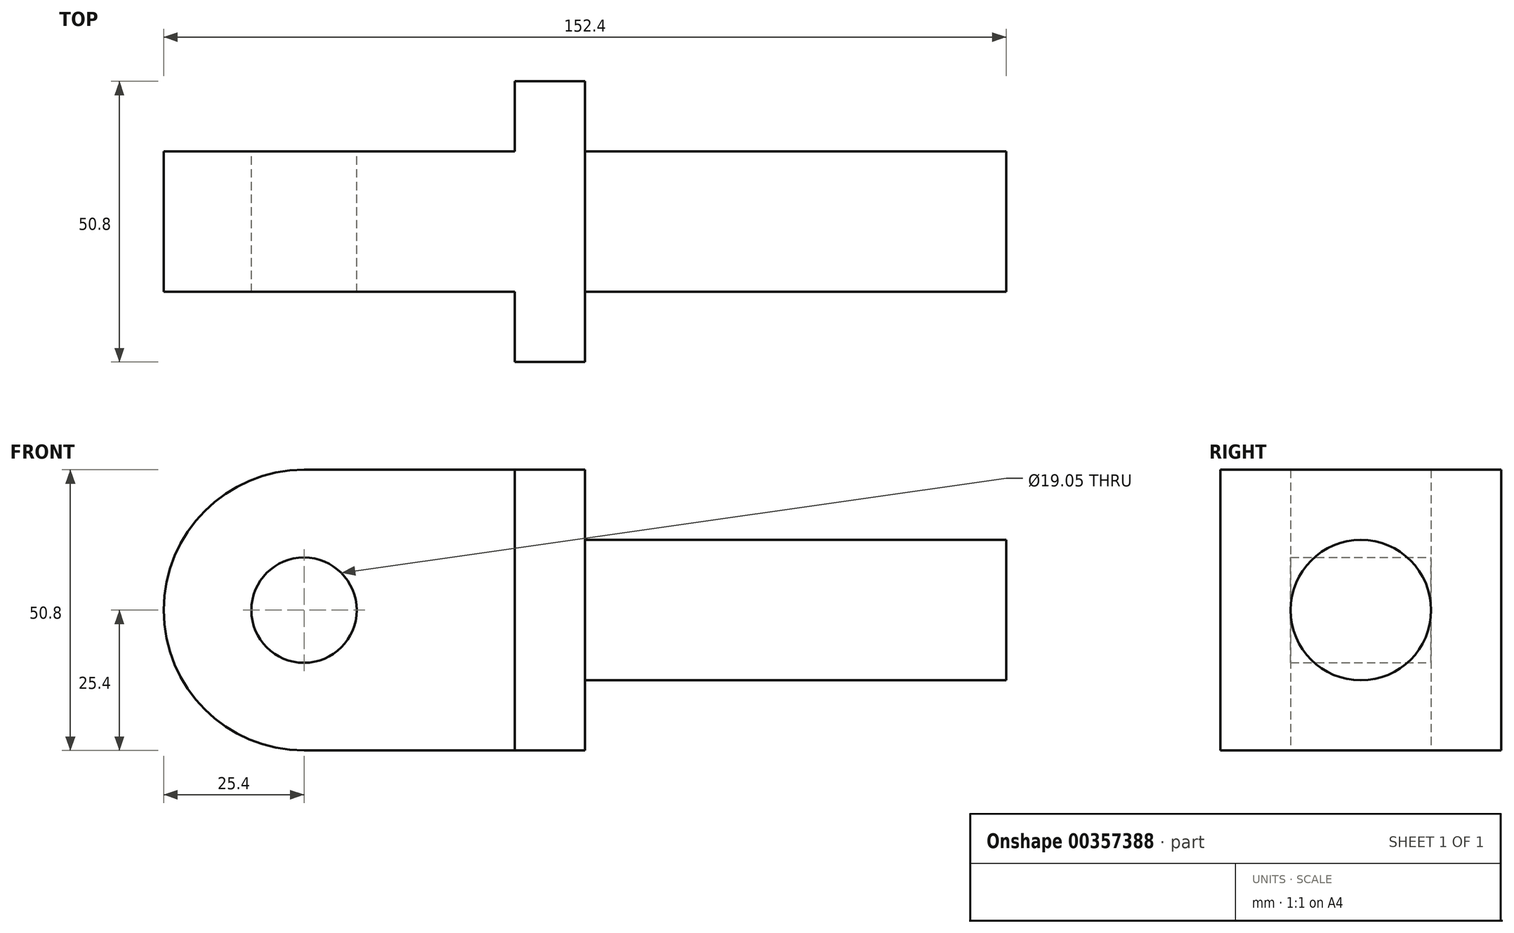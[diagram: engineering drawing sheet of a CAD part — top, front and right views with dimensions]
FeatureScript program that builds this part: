
annotation { "Feature Type Name" : "Feature", "Feature Type Description" : "" }
export const myFeature = defineFeature(function(context is Context, id is Id, definition is map)
    precondition{}
    {
        {
            var Q0;
            Q0=qCreatedBy(makeId("Front.planeOp"),FACE);
            var sketch = newSketch(context, id + "F0", { "sketchPlane" : qUnion([Q0])});
            skCircle(sketch, "E0", {"center": v(0, 0) * mm, "radius": 9.53 * mm});
            skCircle(sketch, "E1", {"center": v(0, 0) * mm, "radius": 25.4 * mm});
            skLineSegment(sketch, "E2.bottom", {"start": v(50.8, 25.4) * mm, "end": v(0, 25.4) * mm});
            skLineSegment(sketch, "E2.top", {"start": v(50.8, -25.4) * mm, "end": v(0, -25.4) * mm});
            skLineSegment(sketch, "E2.left", {"start": v(50.8, 25.4) * mm, "end": v(50.8, -25.4) * mm});
            skLineSegment(sketch, "E3.bottom", {"start": v(50.8, 25.4) * mm, "end": v(38.1, 25.4) * mm});
            skLineSegment(sketch, "E3.top", {"start": v(50.8, -25.4) * mm, "end": v(38.1, -25.4) * mm});
            skLineSegment(sketch, "E3.right", {"start": v(38.1, 25.4) * mm, "end": v(38.1, -25.4) * mm});
            skSolve(sketch);
        }
        {
            var Q0;
            Q0=makeQuery(id+"F0.imprint","IMPRINT",FACE,{"disambiguationData":[TD([[makeQuery(id+"F0.imprint","IMPRINT",EDGE,{"derivedFrom":sQuery(id+"F0.wireOp",EDGE,"E0")}),-1.0]])]});
            var Q1;
            {var subQ0=sQuery(id+"F0.wireOp",EDGE,"E2.bottom");Q1=makeQuery(id+"F0.imprint","IMPRINT",FACE,{"disambiguationData":[TD([[makeQuery(id+"F0.imprint","IMPRINT",EDGE,{"derivedFrom":subQ0}),1.0]])]});}
            var Q2;
            Q2=makeQuery(id+"F0.imprint","IMPRINT",FACE,{"disambiguationData":[TD([[makeQuery(id+"F0.imprint","IMPRINT",EDGE,{"derivedFrom":sQuery(id+"F0.wireOp",EDGE,"E3.bottom")}),1.0]])]});
            extrude(context, id + "F1", {"entities" : qUnion([Q0, Q1, Q2]), "endBound" : BoundingType.SYMMETRIC, "depth" : 25.4 * mm});
        }
        {
            var Q0;
            Q0=makeQuery(id+"F1.opExtrude","CAP_FACE",FACE,{"disambiguationData":[OSD([sQuery(id+"F0.wireOp",EDGE,"E0"),sQuery(id+"F0.wireOp",EDGE,"E1"),sQuery(id+"F0.wireOp",EDGE,"E2.bottom"),sQuery(id+"F0.wireOp",EDGE,"E2.top"),sQuery(id+"F0.wireOp",EDGE,"E3.bottom"),sQuery(id+"F0.wireOp",EDGE,"E3.top"),sQuery(id+"F0.wireOp",EDGE,"E2.left")])],"isStart":false});
            var sketch = newSketch(context, id + "F2", { "sketchPlane" : qUnion([Q0])});
            skLineSegment(sketch, "E4.bottom", {"start": v(50.8, 25.4) * mm, "end": v(38.1, 25.4) * mm});
            skLineSegment(sketch, "E4.top", {"start": v(50.8, -25.4) * mm, "end": v(38.1, -25.4) * mm});
            skLineSegment(sketch, "E4.left", {"start": v(50.8, 25.4) * mm, "end": v(50.8, -25.4) * mm});
            skLineSegment(sketch, "E4.right", {"start": v(38.1, 25.4) * mm, "end": v(38.1, -25.4) * mm});
            skSolve(sketch);
        }
        {
            var Q0;
            Q0=makeQuery(id+"F2.imprint","IMPRINT",FACE,{"disambiguationData":[TD([[makeQuery(id+"F2.imprint","IMPRINT",EDGE,{"derivedFrom":sQuery(id+"F2.wireOp",EDGE,"E4.bottom")}),1.0]])]});
            extrude(context, id + "F3", {"entities" : qUnion([Q0]), "operationType" : NewBodyOperationType.ADD, "depth" : 12.7 * mm});
        }
        {
            var Q0;
            Q0=makeQuery(id+"F1.opExtrude","CAP_FACE",FACE,{"disambiguationData":[OSD([sQuery(id+"F0.wireOp",EDGE,"E0"),sQuery(id+"F0.wireOp",EDGE,"E1"),sQuery(id+"F0.wireOp",EDGE,"E2.bottom"),sQuery(id+"F0.wireOp",EDGE,"E2.top"),sQuery(id+"F0.wireOp",EDGE,"E3.bottom"),sQuery(id+"F0.wireOp",EDGE,"E3.top"),sQuery(id+"F0.wireOp",EDGE,"E2.left")])],"isStart":true});
            var sketch = newSketch(context, id + "F4", { "sketchPlane" : qUnion([Q0])});
            skLineSegment(sketch, "E5.bottom", {"start": v(-50.8, 25.4) * mm, "end": v(-38.1, 25.4) * mm});
            skLineSegment(sketch, "E5.top", {"start": v(-50.8, -25.4) * mm, "end": v(-38.1, -25.4) * mm});
            skLineSegment(sketch, "E5.left", {"start": v(-50.8, 25.4) * mm, "end": v(-50.8, -25.4) * mm});
            skLineSegment(sketch, "E5.right", {"start": v(-38.1, 25.4) * mm, "end": v(-38.1, -25.4) * mm});
            skSolve(sketch);
        }
        {
            var Q0;
            Q0 = qSketchRegion(id + "F4", true);
            extrude(context, id + "F5", {"entities" : qUnion([Q0]), "operationType" : NewBodyOperationType.ADD, "depth" : 12.7 * mm});
        }
        {
            var Q0;
            Q0=makeQuery(id+"F5.boolean.opBoolean","MERGE",FACE,{"derivedFrom":[makeQuery(id+"F3.boolean.opBoolean","MERGE",FACE,{"derivedFrom":[makeQuery(id+"F1.opExtrude","SWEPT_FACE",FACE,{"disambiguationData":[OSD([sQuery(id+"F0.wireOp",EDGE,"E2.left")])]}),makeQuery(id+"F3.opExtrude","SWEPT_FACE",FACE,{"disambiguationData":[OSD([sQuery(id+"F2.wireOp",EDGE,"E4.left")])]})]}),makeQuery(id+"F5.opExtrude","SWEPT_FACE",FACE,{"disambiguationData":[OSD([sQuery(id+"F4.wireOp",EDGE,"E5.left")])]})]});
            var sketch = newSketch(context, id + "F6", { "sketchPlane" : qUnion([Q0])});
            skCircle(sketch, "E6", {"center": v(0, 0) * mm, "radius": 12.7 * mm});
            skSolve(sketch);
        }
        {
            var Q0;
            Q0 = qSketchRegion(id + "F6", true);
            extrude(context, id + "F7", {"entities" : qUnion([Q0]), "operationType" : NewBodyOperationType.ADD, "depth" : 76.2 * mm});
        }
    });
